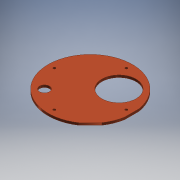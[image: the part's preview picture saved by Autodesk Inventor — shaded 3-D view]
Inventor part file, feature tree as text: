
AUTODESK INVENTOR PART (.ipt)
format: ipt  version: 2018 (Build 220112000, 112)  size: 152,576 bytes
history: native  units: in
note: dims shown in document units (in); Inventor stores cm internally (conversion verified against a paired STEP export)
features: sketch x5, extrude x3, hole x1
ambient origin geometry x8: Origin, YZ Plane, XZ Plane, XY Plane, X Axis, Y Axis, Z Axis, Center Point
bodies: Solid1 (feature_tree)
feature tree (9):
  extrude  "Extrusion1"  TaperAngle=135.0deg  [1 undecoded]
  extrude  "Extrusion2"  Depth=2.25in
  sketch  "Sketch9"  dims[d4=45.0deg d5=1.1in]
  hole  "Hole4"  [1 undecoded]
  extrude  "Extrusion3"  TaperAngle=315.0deg  [1 undecoded]
  sketch  "Sketch1"  dims[d0=3.6in d1=135.0deg]
  sketch  "Sketch2"  dims[d2=3.8in d3=2.25in]
  sketch  "Sketch10"  dims[d6=1.35in d7=315.0deg]
  sketch  "Sketch11"  dims[d8=9.375in d9=0.25in d10=0.0in d11=0.0in d12=0.0in d81=5.0in d82=5.0in d83=8.0in d84=1.5748in d86=360.0deg d88=0.266in d89=0.75in d90=0.507in d91=0.25in d92=0.5635in d93=1.0in d94=0.8108in d95=45.0deg d96=1.75in d97=0.0in]
note: 3 required parameter values undecoded (feature->parameter linkage not recoverable at this tier; creation-order binding heuristic only, values carry confidence <= 0.55)
